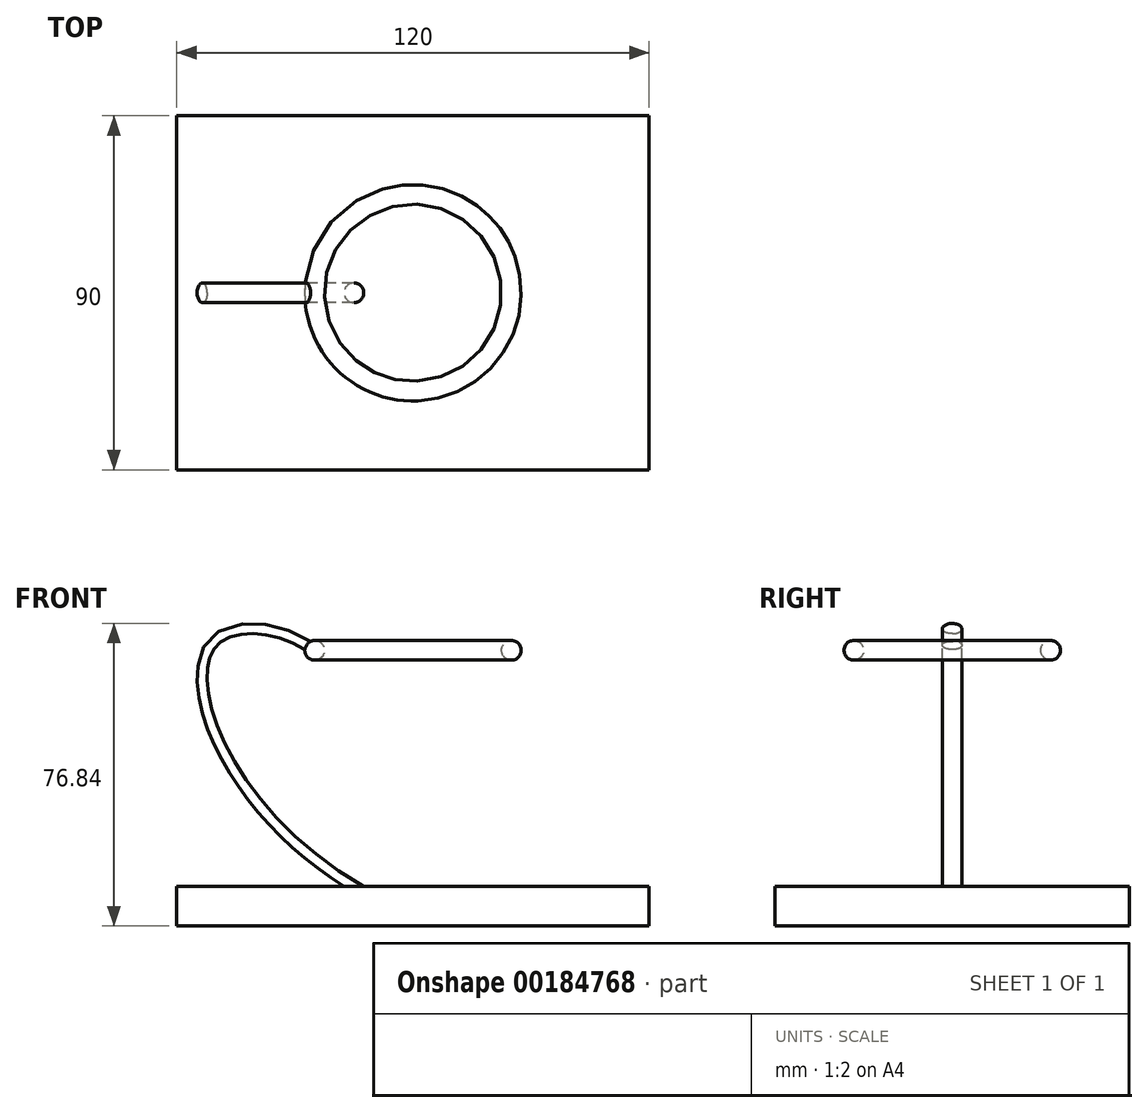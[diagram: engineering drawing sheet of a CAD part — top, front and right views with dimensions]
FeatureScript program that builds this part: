
annotation { "Feature Type Name" : "Feature", "Feature Type Description" : "" }
export const myFeature = defineFeature(function(context is Context, id is Id, definition is map)
    precondition{}
    {
        {
            var Q0;
            Q0=qCreatedBy(makeId("Top.planeOp"),FACE);
            cPlane(context, id + "F0", {"entities" : qUnion([Q0]), "cplaneType" : CPlaneType.OFFSET, "offset" : 60 * mm, "width" : 150 * mm, "height" : 150 * mm});
        }
        {
            var Q0;
            Q0=qCreatedBy(id+"F0.planeOp",FACE);
            var sketch = newSketch(context, id + "F1", { "sketchPlane" : qUnion([Q0])});
            skCircle(sketch, "E0", {"center": v(0, 0) * mm, "radius": 25 * mm});
            skSolve(sketch);
        }
        {
            var Q0;
            Q0=qCreatedBy(makeId("Front.planeOp"),FACE);
            var sketch = newSketch(context, id + "F2", { "sketchPlane" : qUnion([Q0])});
            skCircle(sketch, "E1", {"center": v(25, 60) * mm, "radius": 2.5 * mm});
            skSolve(sketch);
        }
        {
            var Q0;
            Q0=makeQuery(id+"F2.imprint","IMPRINT",FACE,{"disambiguationData":[TD([[makeQuery(id+"F2.imprint","IMPRINT",EDGE,{"derivedFrom":sQuery(id+"F2.wireOp",EDGE,"E1")}),1.0]])]});
            var Q1;
            Q1=sQuery(id+"F1.wireOp",EDGE,"E0");
            sweep(context, id + "F3", {"profiles" : qUnion([Q0]), "path" : qUnion([Q1])});
        }
        {
            var Q0;
            Q0=qCreatedBy(makeId("Top.planeOp"),FACE);
            var sketch = newSketch(context, id + "F4", { "sketchPlane" : qUnion([Q0])});
            skLineSegment(sketch, "E2.bottom", {"start": v(-60, 45) * mm, "end": v(60, 45) * mm});
            skLineSegment(sketch, "E2.top", {"start": v(-60, -45) * mm, "end": v(60, -45) * mm});
            skLineSegment(sketch, "E2.left", {"start": v(-60, 45) * mm, "end": v(-60, -45) * mm});
            skLineSegment(sketch, "E2.right", {"start": v(60, 45) * mm, "end": v(60, -45) * mm});
            skPoint(sketch, "E2.middle", {"position": v(0, 0) * mm});
            skSolve(sketch);
        }
        {
            var Q0;
            Q0 = qSketchRegion(id + "F4", true);
            extrude(context, id + "F5", {"entities" : qUnion([Q0]), "oppositeDirection" : true, "depth" : 10 * mm});
        }
        {
            var Q0;
            Q0=qCreatedBy(makeId("Front.planeOp"),FACE);
            var sketch = newSketch(context, id + "F6", { "sketchPlane" : qUnion([Q0])});
            skPoint(sketch, "E3", {"position": v(-25, 60) * mm});
            skPoint(sketch, "E4", {"position": v(-15, 0) * mm});
            skFitSpline(sketch, "E5", {"points": [v(-25, 60) * mm, v(-51.07, 61.34) * mm, v(-15, 0) * mm], "startDerivative": vector(-68.93, 49.24) * mm, "endDerivative": vector(152.47, -91.4) * mm});
            skSolve(sketch);
        }
        {
            var Q0;
            Q0=qCreatedBy(makeId("Top.planeOp"),FACE);
            var sketch = newSketch(context, id + "F7", { "sketchPlane" : qUnion([Q0])});
            skCircle(sketch, "E6", {"center": v(-15, 0) * mm, "radius": 2.5 * mm});
            skSolve(sketch);
        }
        {
            var Q0;
            Q0=makeQuery(id+"F7.imprint","IMPRINT",FACE,{"disambiguationData":[TD([[makeQuery(id+"F7.imprint","IMPRINT",EDGE,{"derivedFrom":sQuery(id+"F7.wireOp",EDGE,"E6")}),1.0]])]});
            var Q1;
            Q1=sQuery(id+"F6.wireOp",EDGE,"E5");
            sweep(context, id + "F8", {"operationType" : NewBodyOperationType.ADD, "profiles" : qUnion([Q0]), "path" : qUnion([Q1])});
        }
    });
